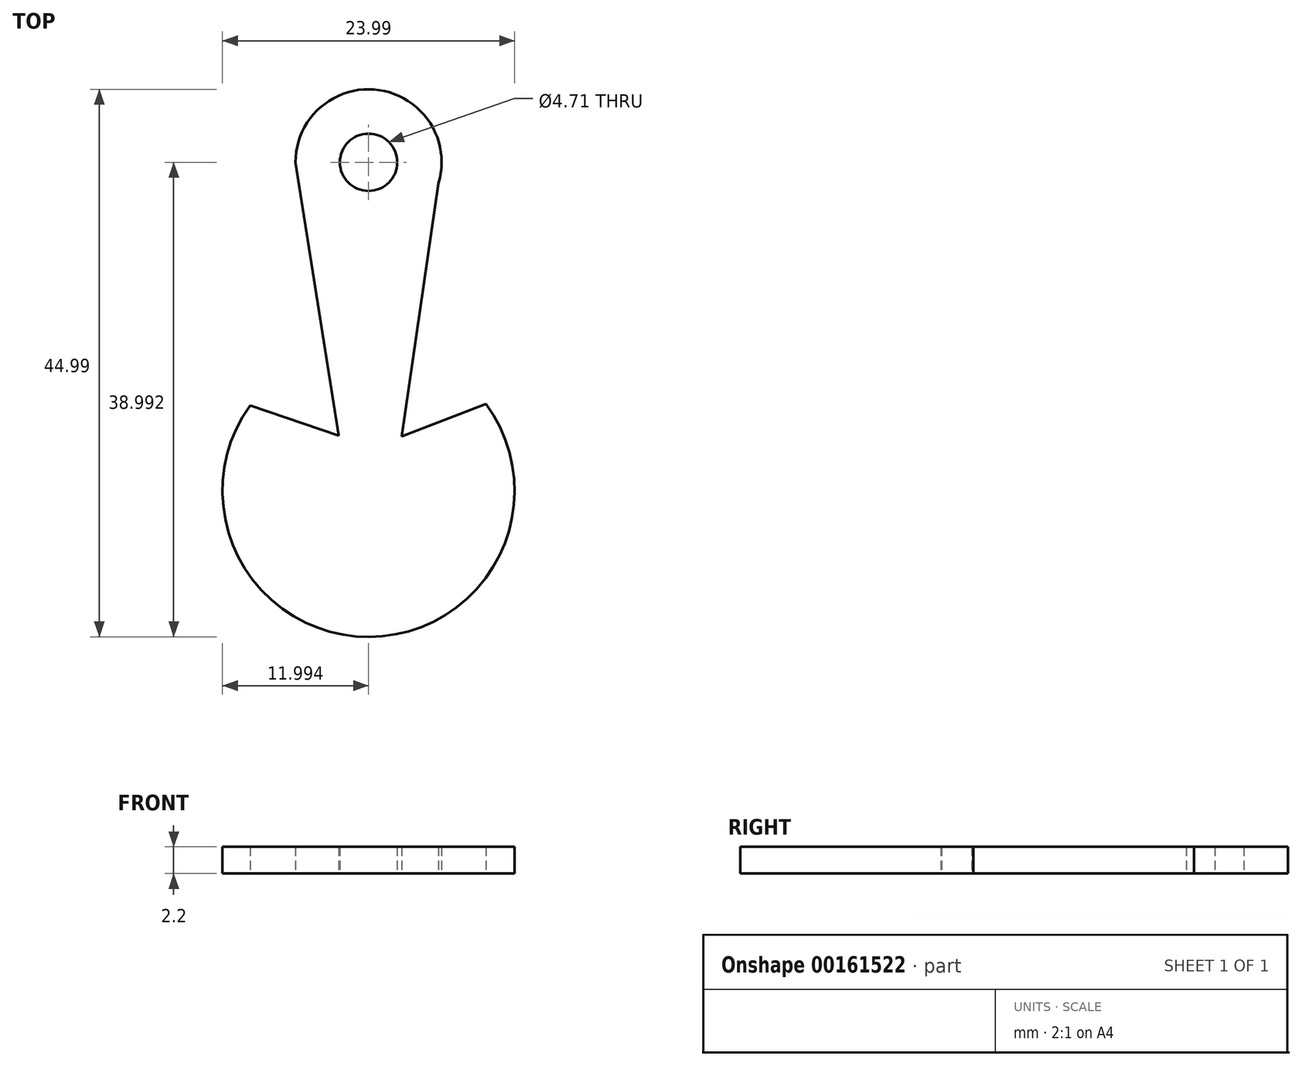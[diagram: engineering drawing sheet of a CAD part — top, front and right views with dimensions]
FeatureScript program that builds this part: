
annotation { "Feature Type Name" : "Feature", "Feature Type Description" : "" }
export const myFeature = defineFeature(function(context is Context, id is Id, definition is map)
    precondition{}
    {
        {
            var Q0;
            Q0=qCreatedBy(makeId("Top.planeOp"),FACE);
            var sketch = newSketch(context, id + "F0", { "sketchPlane" : qUnion([Q0])});
            skArc(sketch, "E0", {"start": v(-24.86, 61.68) * mm, "mid": v(-29.74, 69.33) * mm, "end": v(-36.6, 63.4) * mm});
            skCircle(sketch, "E1", {"center": v(-30.6, 63.4) * mm, "radius": 2.35 * mm});
            skLineSegment(sketch, "E2", {"start": v(-24.86, 61.68) * mm, "end": v(-27.9, 40.86) * mm});
            skLineSegment(sketch, "E3", {"start": v(-36.6, 63.4) * mm, "end": v(-33.05, 40.94) * mm});
            skLineSegment(sketch, "E4", {"start": v(-27.9, 40.86) * mm, "end": v(-20.97, 43.53) * mm});
            skLineSegment(sketch, "E5", {"start": v(-21.12, 43.42) * mm, "end": v(-21.26, 43.42) * mm});
            skLineSegment(sketch, "E6", {"start": v(-33.05, 40.94) * mm, "end": v(-40.33, 43.42) * mm});
            skArc(sketch, "E7.trimOffspring", {"start": v(-40.33, 43.42) * mm, "mid": v(-30.54, 24.4) * mm, "end": v(-20.97, 43.53) * mm});
            skPoint(sketch, "E8.orphan", {"position": v(-24.6, 63.4) * mm});
            skSolve(sketch);
        }
        {
            var Q0;
            Q0=makeQuery(id+"F0.imprint","IMPRINT",FACE,{"disambiguationData":[TD([[makeQuery(id+"F0.imprint","IMPRINT",EDGE,{"derivedFrom":sQuery(id+"F0.wireOp",EDGE,"E0")}),1.0]])]});
            extrude(context, id + "F1", {"entities" : qUnion([Q0]), "depth" : 2.2 * mm});
        }
    });
